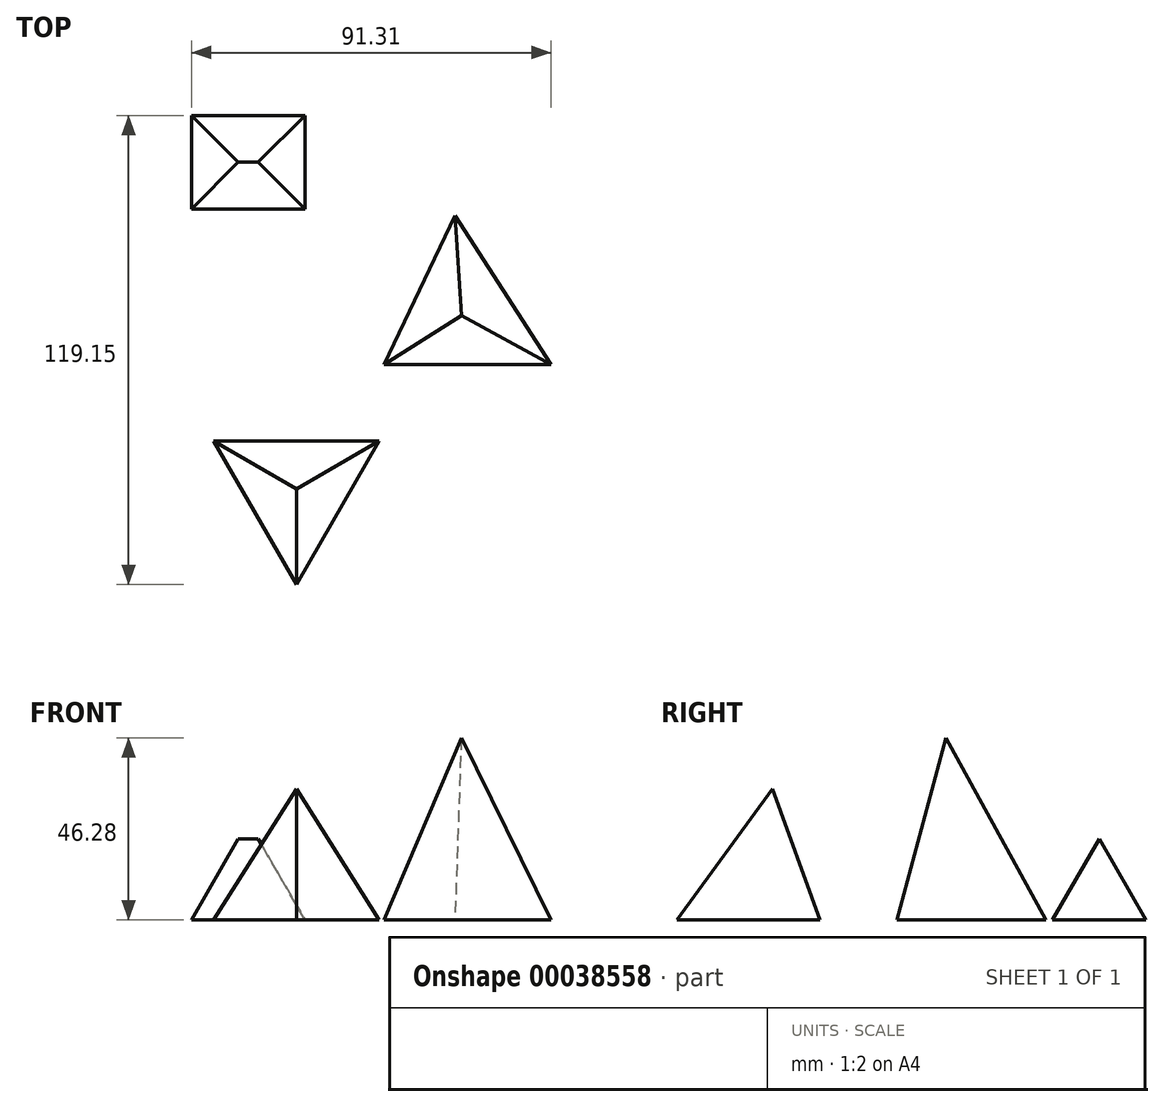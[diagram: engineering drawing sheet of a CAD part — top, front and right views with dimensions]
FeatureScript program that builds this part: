
annotation { "Feature Type Name" : "Feature", "Feature Type Description" : "" }
export const myFeature = defineFeature(function(context is Context, id is Id, definition is map)
    precondition{}
    {
        {
            var Q0;
            Q0=qCreatedBy(makeId("Top.planeOp"),FACE);
            var sketch = newSketch(context, id + "F0", { "sketchPlane" : qUnion([Q0])});
            skLineSegment(sketch, "E0", {"start": v(0, 37.78) * mm, "end": v(-18.02, 0) * mm});
            skLineSegment(sketch, "E1", {"start": v(-18.02, 0) * mm, "end": v(24.4, 0) * mm});
            skLineSegment(sketch, "E2", {"start": v(24.4, 0) * mm, "end": v(0, 37.78) * mm});
            skSolve(sketch);
        }
        {
            var Q0;
            Q0=makeQuery(id+"F0.imprint","IMPRINT",FACE,{"disambiguationData":[TD([[makeQuery(id+"F0.imprint","IMPRINT",EDGE,{"derivedFrom":sQuery(id+"F0.wireOp",EDGE,"E0")}),1.0]])]});
            extrude(context, id + "F1", {"entities" : qUnion([Q0]), "depth" : 50.8 * mm, "hasDraft" : true, "draftAngle" : 15 * degree, "draftPullDirection" : true});
        }
        {
            var Q0;
            Q0=qCreatedBy(makeId("Top.planeOp"),FACE);
            var sketch = newSketch(context, id + "F2", { "sketchPlane" : qUnion([Q0])});
            skLineSegment(sketch, "E3.bottom", {"start": v(-66.91, 63.24) * mm, "end": v(-38.07, 63.24) * mm});
            skLineSegment(sketch, "E3.top", {"start": v(-66.91, 39.49) * mm, "end": v(-38.07, 39.49) * mm});
            skLineSegment(sketch, "E3.left", {"start": v(-66.91, 63.24) * mm, "end": v(-66.91, 39.49) * mm});
            skLineSegment(sketch, "E3.right", {"start": v(-38.07, 63.24) * mm, "end": v(-38.07, 39.49) * mm});
            skSolve(sketch);
        }
        {
            var Q0;
            Q0=makeQuery(id+"F2.imprint","IMPRINT",FACE,{"disambiguationData":[TD([[makeQuery(id+"F2.imprint","IMPRINT",EDGE,{"derivedFrom":sQuery(id+"F2.wireOp",EDGE,"E3.bottom")}),-1.0]])]});
            extrude(context, id + "F3", {"entities" : qUnion([Q0]), "depth" : 25.4 * mm, "hasDraft" : true, "draftAngle" : 30 * degree, "draftPullDirection" : true});
        }
        {
            var Q0;
            Q0=qCreatedBy(makeId("Top.planeOp"),FACE);
            var sketch = newSketch(context, id + "F4", { "sketchPlane" : qUnion([Q0])});
            skLineSegment(sketch, "E4", {"start": v(-61.26, -19.5) * mm, "end": v(-19.23, -19.5) * mm});
            skLineSegment(sketch, "E5", {"start": v(-61.26, -19.5) * mm, "end": v(-40.24, -55.9) * mm});
            skPoint(sketch, "E5.endSnap0", {"position": v(-40.24, -19.5) * mm});
            skLineSegment(sketch, "E6", {"start": v(-40.24, -55.9) * mm, "end": v(-19.23, -19.5) * mm});
            skSolve(sketch);
        }
        {
            var Q0;
            Q0=makeQuery(id+"F4.imprint","IMPRINT",FACE,{"disambiguationData":[TD([[makeQuery(id+"F4.imprint","IMPRINT",EDGE,{"derivedFrom":sQuery(id+"F4.wireOp",EDGE,"E4")}),-1.0]])]});
            extrude(context, id + "F5", {"entities" : qUnion([Q0]), "depth" : 50.8 * mm, "hasDraft" : true, "draftAngle" : 20 * degree, "draftPullDirection" : true});
        }
    });
